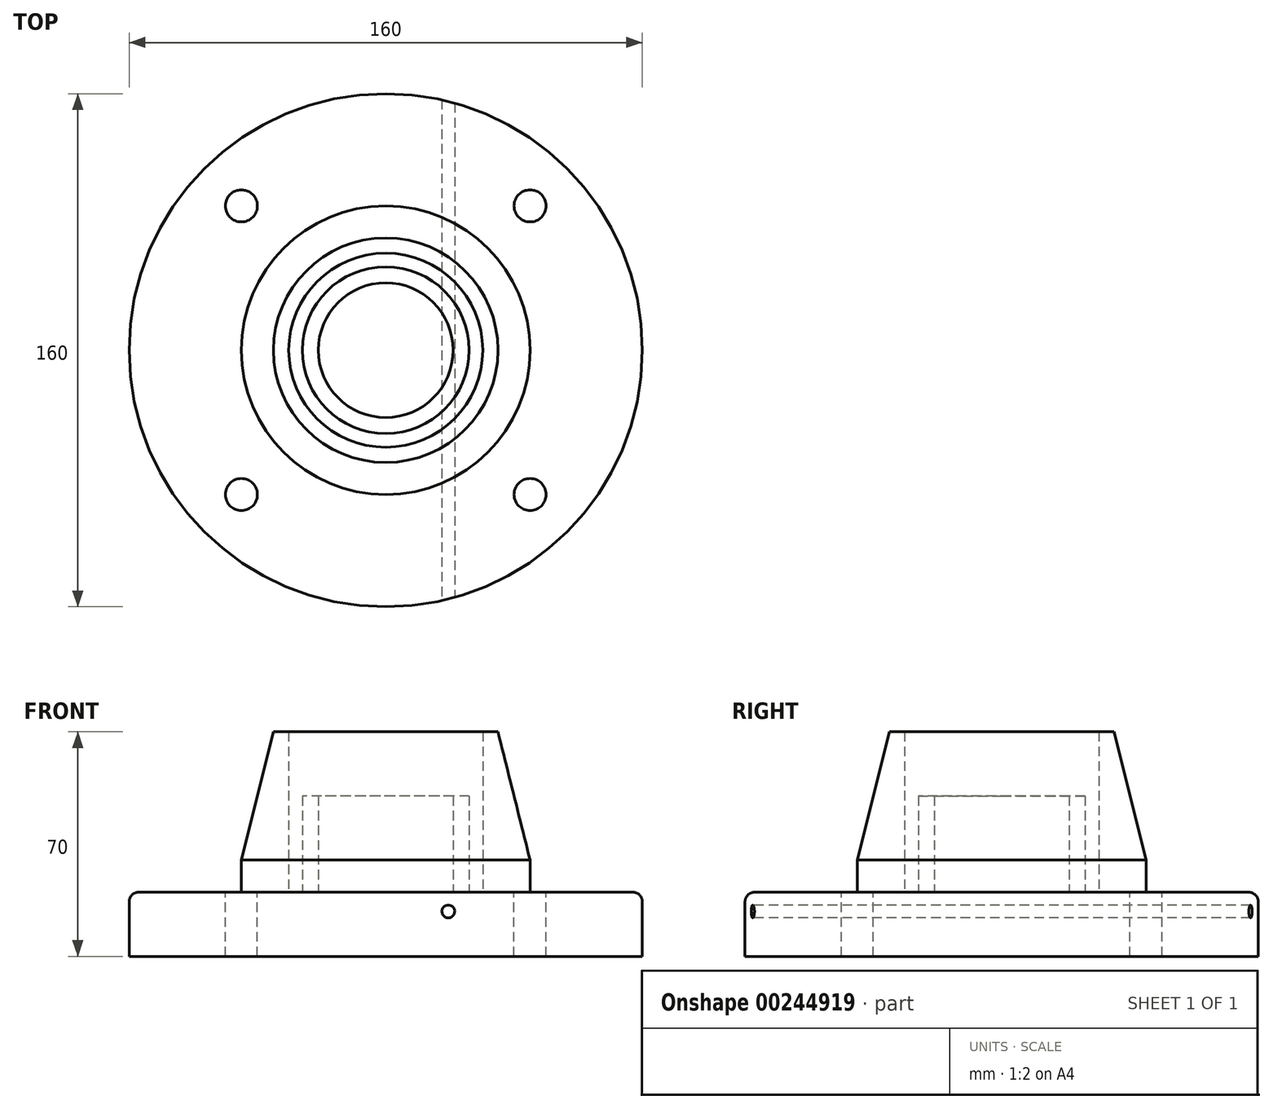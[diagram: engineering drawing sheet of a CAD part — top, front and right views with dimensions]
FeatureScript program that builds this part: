
annotation { "Feature Type Name" : "Feature", "Feature Type Description" : "" }
export const myFeature = defineFeature(function(context is Context, id is Id, definition is map)
    precondition{}
    {
        {
            var Q0;
            Q0=qCreatedBy(makeId("Top.planeOp"),FACE);
            var sketch = newSketch(context, id + "F0", { "sketchPlane" : qUnion([Q0])});
            skCircle(sketch, "E0", {"center": v(0, 0) * mm, "radius": 30.25 * mm});
            skCircle(sketch, "E1", {"center": v(0, 0) * mm, "radius": 45 * mm});
            skSolve(sketch);
        }
        {
            var Q0;
            Q0 = qSketchRegion(id + "F0", true);
            extrude(context, id + "F1", {"entities" : qUnion([Q0]), "depth" : 50 * mm});
        }
        {
            var Q0;
            Q0=qCreatedBy(makeId("Top.planeOp"),FACE);
            var sketch = newSketch(context, id + "F2", { "sketchPlane" : qUnion([Q0])});
            skCircle(sketch, "E2", {"center": v(0, 0) * mm, "radius": 80 * mm});
            skLineSegment(sketch, "E3", {"start": v(0, 0) * mm, "end": v(0, 45) * mm});
            skLineSegment(sketch, "E4", {"start": v(0, 45) * mm, "end": v(45, 45) * mm});
            skCircle(sketch, "E5", {"center": v(45, 45) * mm, "radius": 5 * mm});
            skCircle(sketch, "E6.MirrorC", {"center": v(-45, 45) * mm, "radius": 5 * mm});
            skCircle(sketch, "E7.MirrorC", {"center": v(45, -45) * mm, "radius": 5 * mm});
            skCircle(sketch, "E8.MirrorC", {"center": v(-45, -45) * mm, "radius": 5 * mm});
            skSolve(sketch);
        }
        {
            var Q0;
            Q0 = qSketchRegion(id + "F2", true);
            extrude(context, id + "F3", {"entities" : qUnion([Q0]), "operationType" : NewBodyOperationType.ADD, "oppositeDirection" : true, "depth" : 20 * mm});
        }
        {
            var Q0;
            Q0=qCreatedBy(makeId("Top.planeOp"),FACE);
            var sketch = newSketch(context, id + "F4", { "sketchPlane" : qUnion([Q0])});
            skCircle(sketch, "E9", {"center": v(0, 0) * mm, "radius": 26 * mm});
            skCircle(sketch, "E10", {"center": v(0, 0) * mm, "radius": 21 * mm});
            skSolve(sketch);
        }
        {
            var Q0;
            Q0 = qSketchRegion(id + "F4", true);
            extrude(context, id + "F5", {"entities" : qUnion([Q0]), "operationType" : NewBodyOperationType.ADD, "depth" : 30 * mm});
        }
        {
            var Q0;
            Q0=makeQuery(id+"F1.opExtrude","CAP_EDGE",EDGE,{"disambiguationData":[OSD([sQuery(id+"F0.wireOp",EDGE,"E1")])],"isStart":false});
            chamfer(context, id + "F6", {"entities" : qUnion([Q0]), "chamferType" : ChamferType.TWO_OFFSETS, "width1" : 10 * mm, "oppositeDirection" : false, "width2" : 40 * mm, "tangentPropagation" : true});
        }
        {
            var Q0;
            Q0=qCreatedBy(makeId("Front.planeOp"),FACE);
            var sketch = newSketch(context, id + "F7", { "sketchPlane" : qUnion([Q0])});
            skLineSegment(sketch, "E11", {"start": v(0, 0) * mm, "end": v(0, -6) * mm});
            skLineSegment(sketch, "E12", {"start": v(0, -6) * mm, "end": v(19.5, -6) * mm});
            skCircle(sketch, "E13", {"center": v(19.5, -6) * mm, "radius": 2 * mm});
            skCircle(sketch, "E14.MirrorC", {"center": v(-19.5, -6) * mm, "radius": 2 * mm});
            skSolve(sketch);
        }
        {
            var Q0;
            {Q0=qUnion([makeQuery(id+"F7.imprint","IMPRINT",FACE,{"disambiguationData":[TD([[makeQuery(id+"F7.imprint","IMPRINT",EDGE,{"derivedFrom":sQuery(id+"F7.wireOp",EDGE,"E13")}),1.0]])]}),makeQuery(id+"F7.imprint","IMPRINT",FACE,{"disambiguationData":[TD([[makeQuery(id+"F7.imprint","IMPRINT",EDGE,{"derivedFrom":sQuery(id+"F7.wireOp",EDGE,"E14.MirrorC")}),-1.0]])]})]);}
            extrude(context, id + "F8", {"entities" : qUnion([Q0]), "operationType" : NewBodyOperationType.REMOVE, "endBound" : BoundingType.SYMMETRIC, "oppositeDirection" : true, "depth" : 170 * mm});
        }
        {
            var Q0;
            Q0=makeQuery(id+"F3.opExtrude","CAP_EDGE",EDGE,{"disambiguationData":[OSD([sQuery(id+"F2.wireOp",EDGE,"E2")])],"isStart":true});
            fillet(context, id + "F9", {"entities" : qUnion([Q0]), "radius" : 3 * mm, "tangentPropagation" : true, "allowEdgeOverflow" : false});
        }
    });
